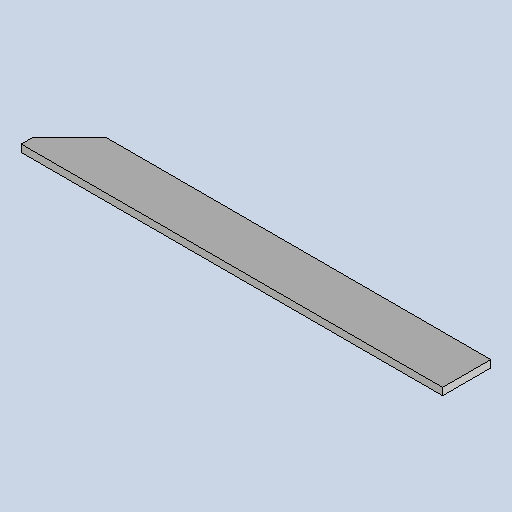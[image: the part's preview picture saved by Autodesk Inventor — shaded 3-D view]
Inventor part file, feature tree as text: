
AUTODESK INVENTOR PART (.ipt)
format: ipt  version: 2025 (Build 290162010, 162A)  size: 106,496 bytes
history: native  units: mm
features: other x2, sheet_metal_op x1, chamfer x1, sketch x1
ambient origin geometry x8: Origin, YZ Plane, XZ Plane, XY Plane, X Axis, Y Axis, Z Axis, Center Point
bodies: Solid1 (feature_tree)
feature tree (5):
  sheet_metal_op  "Face1"
  chamfer  "Chamfer1"  Distance=175.0mm
  sketch  "Sketch1"  dims[d2=20.0mm d3=175.0mm d4=3.0mm d5=15.0mm d6=2.0mm d7=45.0deg]
  other  "Plate1"
  other  "Definition1"
